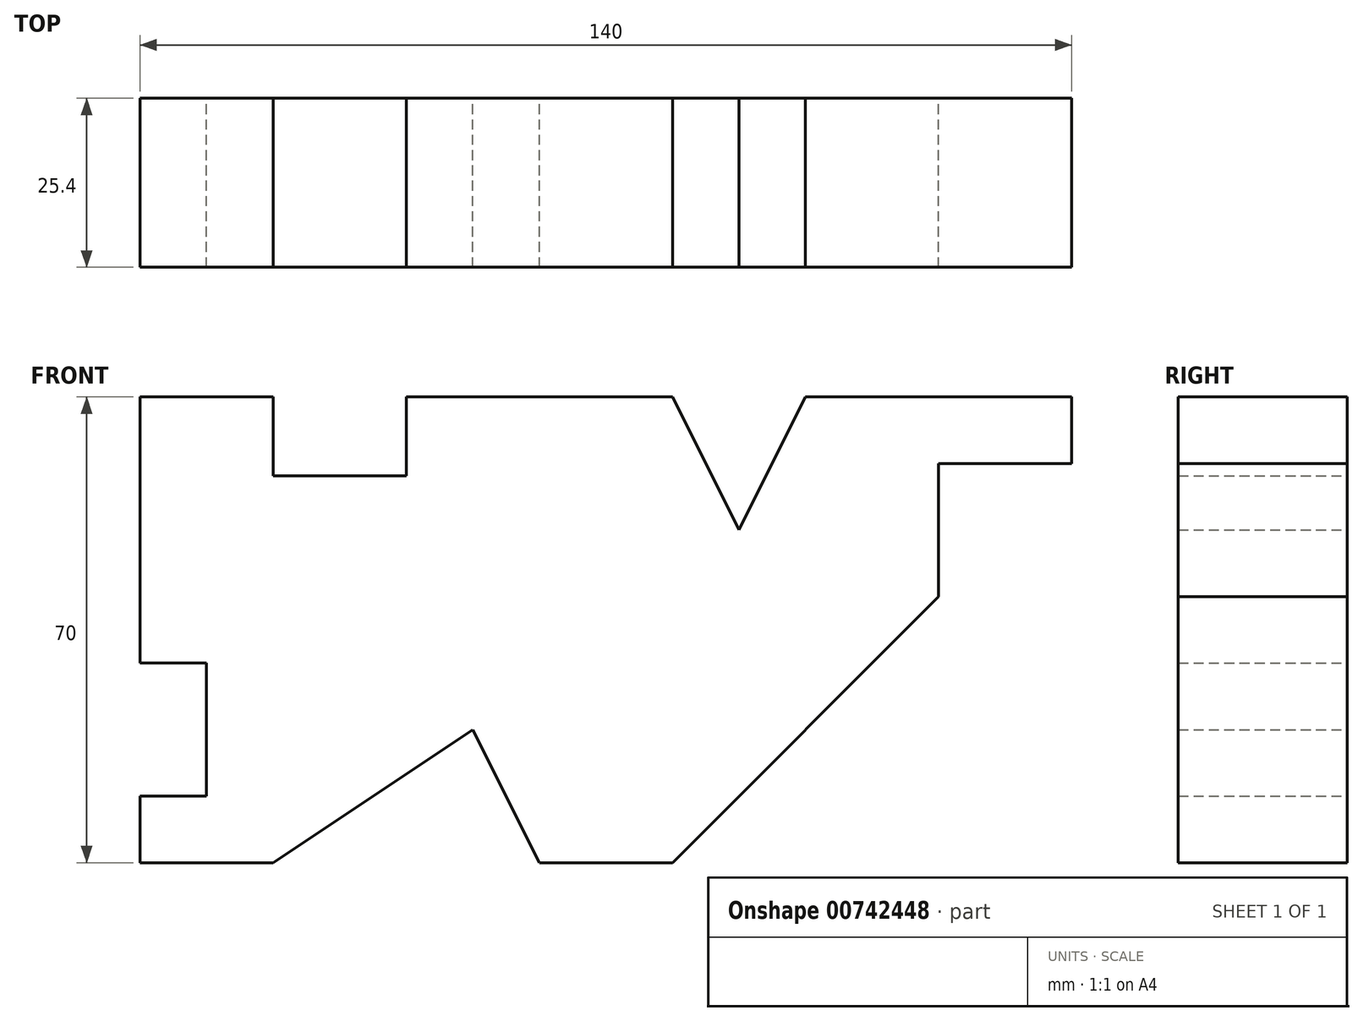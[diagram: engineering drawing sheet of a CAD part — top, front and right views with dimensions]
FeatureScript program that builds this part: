
annotation { "Feature Type Name" : "Feature", "Feature Type Description" : "" }
export const myFeature = defineFeature(function(context is Context, id is Id, definition is map)
    precondition{}
    {
        {
            var Q0;
            Q0=qCreatedBy(makeId("Front.planeOp"),FACE);
            var sketch = newSketch(context, id + "F0", { "sketchPlane" : qUnion([Q0])});
            skLineSegment(sketch, "E0", {"start": v(-80, 60) * mm, "end": v(-60, 60) * mm});
            skLineSegment(sketch, "E1", {"start": v(-60, 60) * mm, "end": v(-60, 48.16) * mm});
            skLineSegment(sketch, "E2", {"start": v(-60, 48.16) * mm, "end": v(-40, 48.16) * mm});
            skLineSegment(sketch, "E3", {"start": v(-40, 48.16) * mm, "end": v(-40, 60) * mm});
            skLineSegment(sketch, "E4", {"start": v(-40, 60) * mm, "end": v(0, 60) * mm});
            skLineSegment(sketch, "E5", {"start": v(0, 60) * mm, "end": v(10, 40) * mm});
            skLineSegment(sketch, "E6", {"start": v(10, 40) * mm, "end": v(20, 60) * mm});
            skLineSegment(sketch, "E7", {"start": v(20, 60) * mm, "end": v(60, 60) * mm});
            skLineSegment(sketch, "E8", {"start": v(60, 60) * mm, "end": v(60, 50) * mm});
            skLineSegment(sketch, "E9", {"start": v(60, 50) * mm, "end": v(40, 50) * mm});
            skLineSegment(sketch, "E10", {"start": v(40, 50) * mm, "end": v(40, 30) * mm});
            skLineSegment(sketch, "E11", {"start": v(40, 30) * mm, "end": v(0, -10) * mm});
            skLineSegment(sketch, "E12", {"start": v(0, -10) * mm, "end": v(-20, -10) * mm});
            skLineSegment(sketch, "E13", {"start": v(-20, -10) * mm, "end": v(-30, 10) * mm});
            skLineSegment(sketch, "E14", {"start": v(-30, 10) * mm, "end": v(-60, -10) * mm});
            skLineSegment(sketch, "E15", {"start": v(-60, -10) * mm, "end": v(-80, -10) * mm});
            skLineSegment(sketch, "E16", {"start": v(-80, -10) * mm, "end": v(-80, 0) * mm});
            skLineSegment(sketch, "E17", {"start": v(-80, 0) * mm, "end": v(-70, 0) * mm});
            skLineSegment(sketch, "E18", {"start": v(-70, 0) * mm, "end": v(-70, 20) * mm});
            skLineSegment(sketch, "E19", {"start": v(-70, 20) * mm, "end": v(-80, 20) * mm});
            skLineSegment(sketch, "E20", {"start": v(-80, 20) * mm, "end": v(-80, 60) * mm});
            skSolve(sketch);
        }
        {
            var Q0;
            Q0=makeQuery(id+"F0.imprint","IMPRINT",FACE,{"disambiguationData":[TD([[makeQuery(id+"F0.imprint","IMPRINT",EDGE,{"derivedFrom":sQuery(id+"F0.wireOp",EDGE,"E0")}),-1.0]])]});
            extrude(context, id + "F1", {"entities" : qUnion([Q0]), "depth" : 25.4 * mm, "offsetDistance" : 25.4 * mm});
        }
    });
